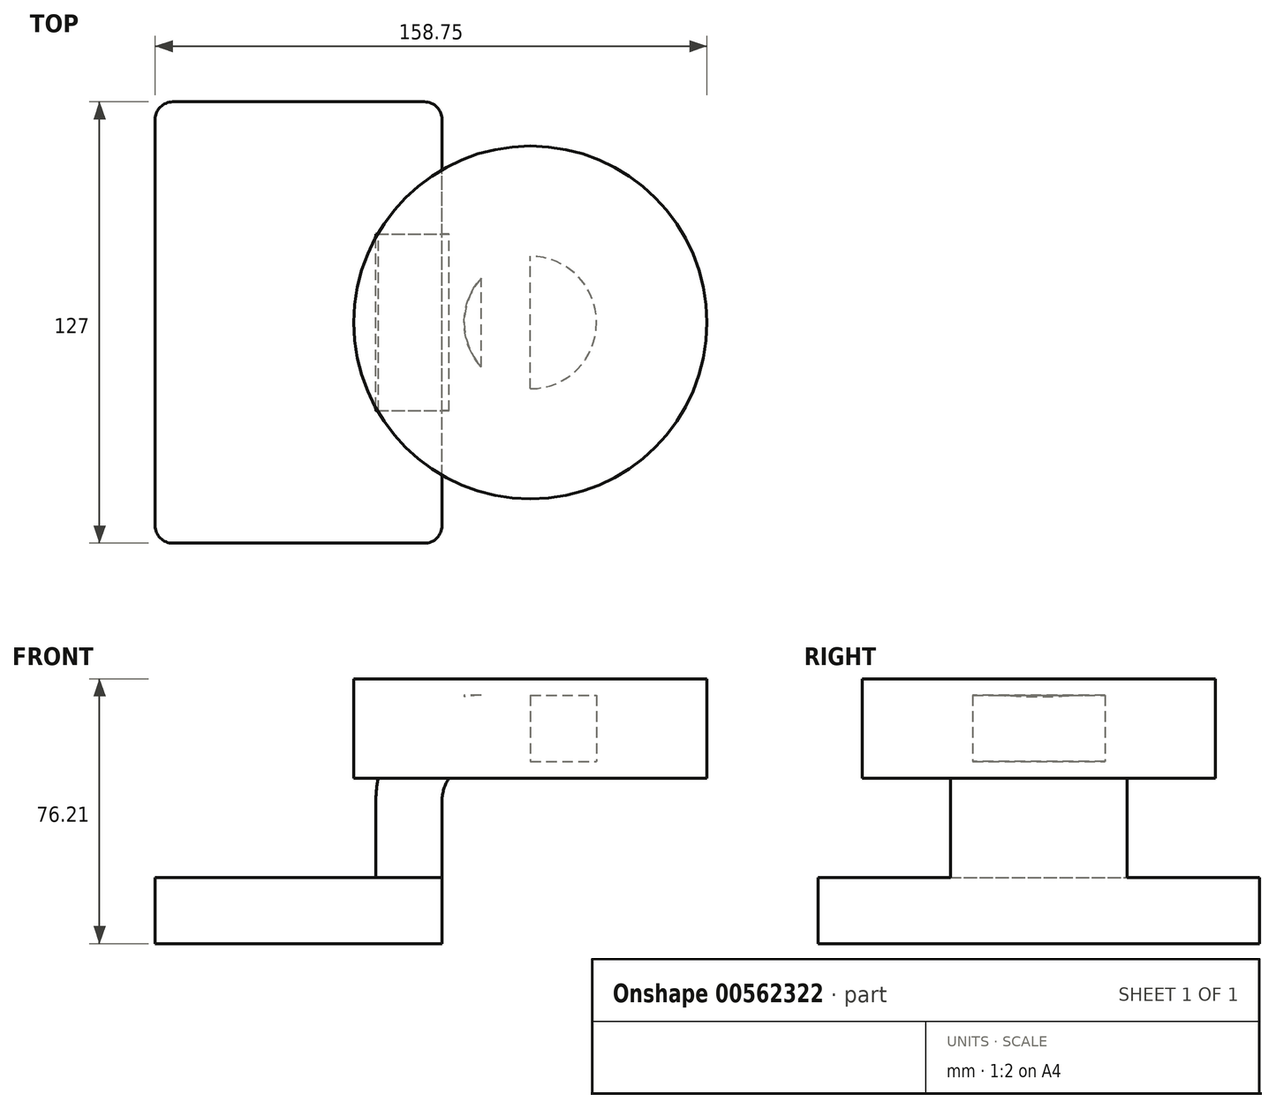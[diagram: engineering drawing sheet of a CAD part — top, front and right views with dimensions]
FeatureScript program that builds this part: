
annotation { "Feature Type Name" : "Feature", "Feature Type Description" : "" }
export const myFeature = defineFeature(function(context is Context, id is Id, definition is map)
    precondition{}
    {
        {
            var Q0;
            Q0=qCreatedBy(makeId("Front.planeOp"),FACE);
            var sketch = newSketch(context, id + "F0", { "sketchPlane" : qUnion([Q0])});
            skLineSegment(sketch, "E0.bottom", {"start": v(-41.28, -9.53) * mm, "end": v(41.28, -9.53) * mm});
            skLineSegment(sketch, "E0.top", {"start": v(-41.28, 9.53) * mm, "end": v(41.28, 9.53) * mm});
            skLineSegment(sketch, "E0.left", {"start": v(-41.28, -9.53) * mm, "end": v(-41.28, 9.53) * mm});
            skLineSegment(sketch, "E0.right", {"start": v(41.28, -9.53) * mm, "end": v(41.28, 9.53) * mm});
            skPoint(sketch, "E0.middle", {"position": v(0, 0) * mm});
            skLineSegment(sketch, "E1.bottom", {"start": v(66.68, 38.1) * mm, "end": v(117.48, 38.1) * mm});
            skLineSegment(sketch, "E1.top", {"start": v(66.68, 66.67) * mm, "end": v(117.48, 66.67) * mm});
            skLineSegment(sketch, "E1.left", {"start": v(66.68, 38.1) * mm, "end": v(66.68, 66.67) * mm});
            skLineSegment(sketch, "E1.right", {"start": v(117.48, 38.1) * mm, "end": v(117.48, 66.67) * mm});
            skPoint(sketch, "E1.middle", {"position": v(92.08, 52.39) * mm});
            skLineSegment(sketch, "E2", {"start": v(41.28, 9.53) * mm, "end": v(41.28, 31.65) * mm});
            skArc(sketch, "E3", {"start": v(41.28, 31.65) * mm, "mid": v(44.56, 39.59) * mm, "end": v(52.5, 42.88) * mm});
            skLineSegment(sketch, "E4", {"start": v(52.5, 42.88) * mm, "end": v(85.73, 42.88) * mm});
            skLineSegment(sketch, "E5.0", {"start": v(52.5, 61.93) * mm, "end": v(85.73, 61.93) * mm});
            skArc(sketch, "E5.1", {"start": v(22.23, 31.65) * mm, "mid": v(31.1, 53.06) * mm, "end": v(52.5, 61.93) * mm});
            skLineSegment(sketch, "E5.2", {"start": v(22.22, 9.53) * mm, "end": v(22.22, 31.65) * mm});
            skLineSegment(sketch, "E6", {"start": v(85.73, 42.88) * mm, "end": v(85.73, 61.93) * mm});
            skFitSpline(sketch, "E7", {"points": [v(-41.28, 9.53) * mm, v(52.5, 61.93) * mm], "startDerivative": vector(-2.95, 97.74) * mm, "endDerivative": vector(203.6, -2.88) * mm});
            skSolve(sketch);
        }
        {
            var Q0;
            Q0=makeQuery(id+"F0.imprint","IMPRINT",FACE,{"disambiguationData":[TD([[makeQuery(id+"F0.imprint","IMPRINT",EDGE,{"derivedFrom":sQuery(id+"F0.wireOp",EDGE,"E0.bottom")}),1.0]])]});
            extrude(context, id + "F1", {"entities" : qUnion([Q0]), "endBound" : BoundingType.SYMMETRIC, "depth" : 127 * mm, "offsetDistance" : 25.4 * mm});
        }
        {
            var Q0;
            {var subQ0=sQuery(id+"F0.wireOp",EDGE,"E2");Q0=makeQuery(id+"F0.imprint","IMPRINT",FACE,{"disambiguationData":[TD([[makeQuery(id+"F0.imprint","IMPRINT",EDGE,{"derivedFrom":subQ0}),1.0]])]});}
            var Q1;
            Q1=sQuery(id+"F0.wireOp",EDGE,"E5.2");
            extrude(context, id + "F2", {"entities" : qUnion([Q0]), "operationType" : NewBodyOperationType.ADD, "surfaceEntities" : qUnion([Q1]), "endBound" : BoundingType.SYMMETRIC, "depth" : 50.8 * mm, "offsetDistance" : 25.4 * mm});
        }
        {
            var Q0;
            Q0=makeQuery(id+"F0.imprint","IMPRINT",FACE,{"disambiguationData":[TD([[makeQuery(id+"F0.imprint","IMPRINT",EDGE,{"derivedFrom":sQuery(id+"F0.wireOp",EDGE,"E5.1")}),1.0]])]});
            extrude(context, id + "F3", {"entities" : qUnion([Q0]), "operationType" : NewBodyOperationType.ADD, "depth" : 15.88 * mm, "offsetDistance" : 25.4 * mm});
        }
        {
            var Q0;
            {var subQ4=sQuery(id+"F0.wireOp",EDGE,"E1.bottom");Q0=makeQuery(id+"F0.imprint","IMPRINT",FACE,{"disambiguationData":[TD([[makeQuery(id+"F0.imprint","IMPRINT",EDGE,{"derivedFrom":subQ4}),1.0]])]});}
            var Q1;
            Q1=sQuery(id+"F0.wireOp",EDGE,"E1.left");
            revolve(context, id + "F4", {"operationType" : NewBodyOperationType.ADD, "entities" : qUnion([Q0]), "axis" : qUnion([Q1]), "revolveType" : RevolveType.FULL});
        }
        {
            var Q0;
            Q0=makeQuery(id+"F1.opExtrude","CAP_EDGE",EDGE,{"disambiguationData":[OSD([sQuery(id+"F0.wireOp",EDGE,"E0.right")])],"isStart":false});
            var Q1;
            Q1=makeQuery(id+"F1.opExtrude","CAP_EDGE",EDGE,{"disambiguationData":[OSD([sQuery(id+"F0.wireOp",EDGE,"E0.left")])],"isStart":false});
            var Q2;
            Q2=makeQuery(id+"F1.opExtrude","CAP_EDGE",EDGE,{"disambiguationData":[OSD([sQuery(id+"F0.wireOp",EDGE,"E0.right")])],"isStart":true});
            var Q3;
            Q3=makeQuery(id+"F1.opExtrude","CAP_EDGE",EDGE,{"disambiguationData":[OSD([sQuery(id+"F0.wireOp",EDGE,"E0.left")])],"isStart":true});
            fillet(context, id + "F5", {"entities" : qUnion([Q0, Q1, Q2, Q3]), "radius" : 5.08 * mm, "tangentPropagation" : true, "allowEdgeOverflow" : false});
        }
    });
